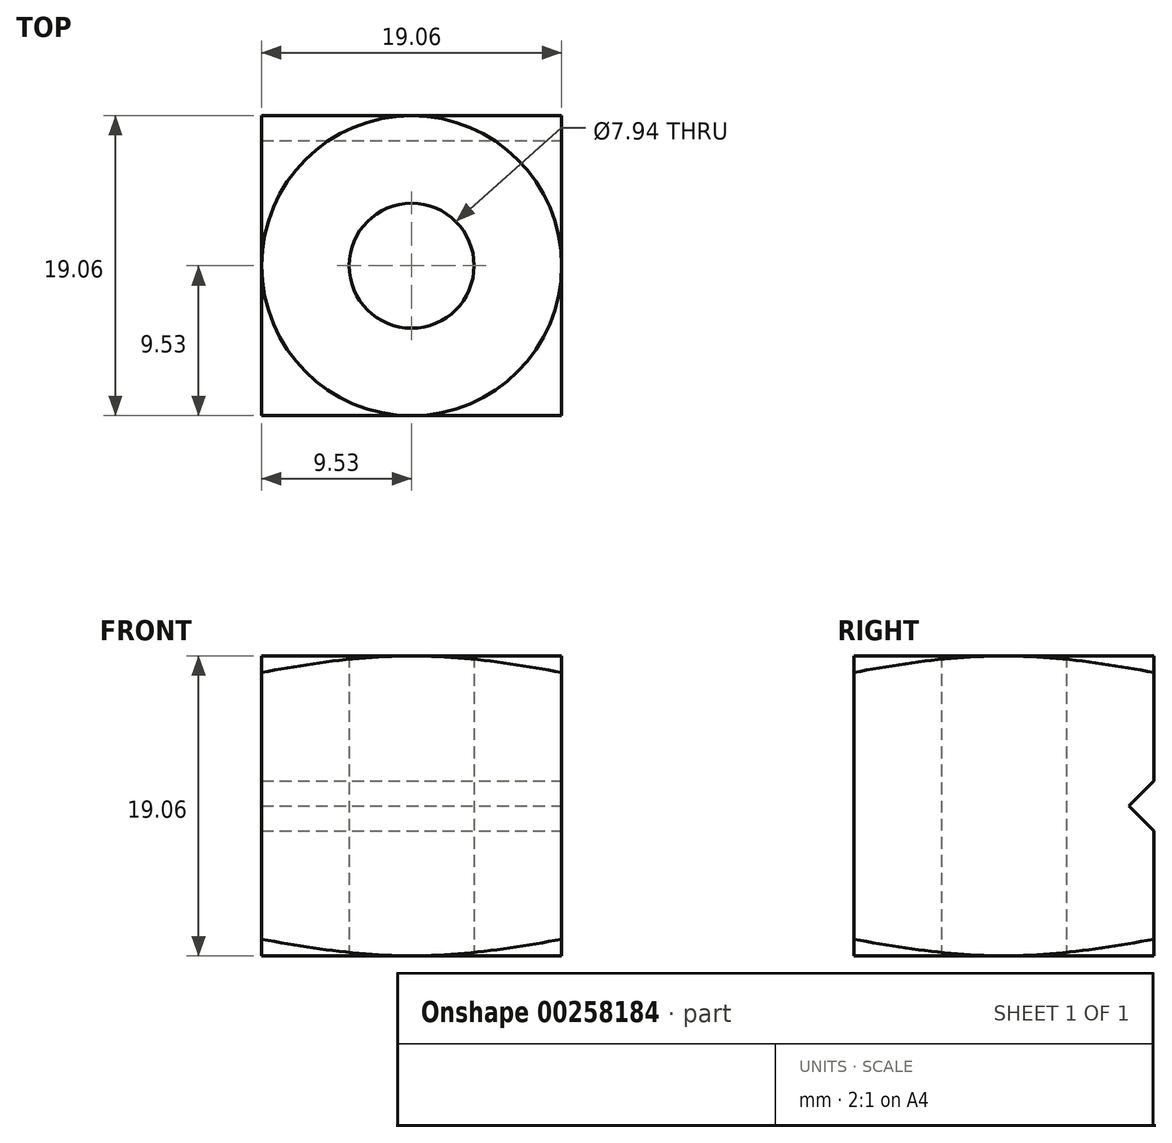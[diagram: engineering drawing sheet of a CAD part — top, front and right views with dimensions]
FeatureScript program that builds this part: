
annotation { "Feature Type Name" : "Feature", "Feature Type Description" : "" }
export const myFeature = defineFeature(function(context is Context, id is Id, definition is map)
    precondition{}
    {
        {
            var Q0;
            Q0=qCreatedBy(makeId("Top.planeOp"),FACE);
            var sketch = newSketch(context, id + "F0", { "sketchPlane" : qUnion([Q0])});
            skLineSegment(sketch, "E0.bottom", {"start": v(-9.52, 9.53) * mm, "end": v(9.53, 9.53) * mm});
            skLineSegment(sketch, "E0.top", {"start": v(-9.53, -9.53) * mm, "end": v(9.52, -9.53) * mm});
            skLineSegment(sketch, "E0.left", {"start": v(-9.52, 9.53) * mm, "end": v(-9.53, -9.53) * mm});
            skLineSegment(sketch, "E0.right", {"start": v(9.53, 9.53) * mm, "end": v(9.52, -9.53) * mm});
            skPoint(sketch, "E0.middle", {"position": v(0, 0) * mm});
            skCircle(sketch, "E1", {"center": v(0, 0) * mm, "radius": 3.97 * mm});
            skSolve(sketch);
        }
        {
            var Q0;
            Q0=makeQuery(id+"F0.imprint","IMPRINT",FACE,{"disambiguationData":[TD([[makeQuery(id+"F0.imprint","IMPRINT",EDGE,{"derivedFrom":sQuery(id+"F0.wireOp",EDGE,"E0.bottom")}),-1.0]])]});
            extrude(context, id + "F1", {"entities" : qUnion([Q0]), "depth" : 9.52 * mm});
        }
        {
            var Q0;
            Q0=makeQuery(id+"F1.opExtrude","CAP_FACE",FACE,{"disambiguationData":[OSD([sQuery(id+"F0.wireOp",EDGE,"E0.bottom"),sQuery(id+"F0.wireOp",EDGE,"E0.top"),sQuery(id+"F0.wireOp",EDGE,"E0.left"),sQuery(id+"F0.wireOp",EDGE,"E0.right"),sQuery(id+"F0.wireOp",EDGE,"E1")])],"isStart":false});
            var sketch = newSketch(context, id + "F2", { "sketchPlane" : qUnion([Q0])});
            skCircle(sketch, "E2", {"center": v(0, 0) * mm, "radius": 9.53 * mm});
            skSolve(sketch);
        }
        {
            var Q0;
            Q0=qCreatedBy(makeId("Right.planeOp"),FACE);
            var sketch = newSketch(context, id + "F3", { "sketchPlane" : qUnion([Q0])});
            skLineSegment(sketch, "E3.0.0", {"start": v(-9.53, 9.53) * mm, "end": v(0, 9.53) * mm});
            skLineSegment(sketch, "E3.0.1", {"start": v(0, 9.53) * mm, "end": v(9.53, 9.53) * mm});
            skLineSegment(sketch, "E3.0.2", {"start": v(9.53, 9.53) * mm, "end": v(0, 9.53) * mm});
            skLineSegment(sketch, "E3.0.3", {"start": v(0, 9.53) * mm, "end": v(-9.53, 9.53) * mm});
            skLineSegment(sketch, "E4", {"start": v(-9.53, 9.53) * mm, "end": v(-14.47, 9.53) * mm});
            skLineSegment(sketch, "E5", {"start": v(-14.47, 9.53) * mm, "end": v(-14.47, 8.2) * mm});
            skLineSegment(sketch, "E6", {"start": v(-14.47, 8.2) * mm, "end": v(-9.53, 9.53) * mm});
            skSolve(sketch);
        }
        {
            var Q0;
            Q0=makeQuery(id+"F3.imprint","IMPRINT",FACE,{"disambiguationData":[TD([[makeQuery(id+"F3.imprint","IMPRINT",EDGE,{"derivedFrom":sQuery(id+"F3.wireOp",EDGE,"E4")}),1.0]])]});
            var Q1;
            Q1=sQuery(id+"F2.wireOp",EDGE,"E2");
            sweep(context, id + "F4", {"operationType" : NewBodyOperationType.REMOVE, "profiles" : qUnion([Q0]), "path" : qUnion([Q1])});
        }
        {
            var Q0;
            Q0=makeQuery(id+"F1.opExtrude","SWEPT_FACE",FACE,{"disambiguationData":[OSD([sQuery(id+"F0.wireOp",EDGE,"E0.right")])]});
            var sketch = newSketch(context, id + "F5", { "sketchPlane" : qUnion([Q0])});
            skLineSegment(sketch, "E7", {"start": v(9.53, 0) * mm, "end": v(7.94, 0) * mm});
            skLineSegment(sketch, "E8", {"start": v(7.94, 0) * mm, "end": v(9.53, 1.59) * mm});
            skLineSegment(sketch, "E9", {"start": v(9.53, 1.59) * mm, "end": v(9.53, 0) * mm});
            skSolve(sketch);
        }
        {
            var Q0;
            Q0 = qSketchRegion(id + "F5", true);
            extrude(context, id + "F6", {"entities" : qUnion([Q0]), "operationType" : NewBodyOperationType.REMOVE, "endBound" : BoundingType.THROUGH_ALL, "oppositeDirection" : true, "depth" : 25.4 * mm});
        }
        {
            var Q0;
            Q0=makeQuery(id+"F1.opExtrude","SWEPT_BODY",BODY,{"disambiguationData":[OSD([sQuery(id+"F0.wireOp",EDGE,"E0.bottom"),sQuery(id+"F0.wireOp",EDGE,"E0.top"),sQuery(id+"F0.wireOp",EDGE,"E0.left"),sQuery(id+"F0.wireOp",EDGE,"E0.right"),sQuery(id+"F0.wireOp",EDGE,"E1")])]});
            var Q1;
            Q1=makeQuery(id+"F1.opExtrude","CAP_FACE",FACE,{"disambiguationData":[OSD([sQuery(id+"F0.wireOp",EDGE,"E0.bottom"),sQuery(id+"F0.wireOp",EDGE,"E0.top"),sQuery(id+"F0.wireOp",EDGE,"E0.left"),sQuery(id+"F0.wireOp",EDGE,"E0.right"),sQuery(id+"F0.wireOp",EDGE,"E1")])],"isStart":true});
            mirror(context, id + "F7", {"operationType" : NewBodyOperationType.ADD, "entities" : qUnion([Q0]), "mirrorPlane" : qUnion([Q1])});
        }
    });
